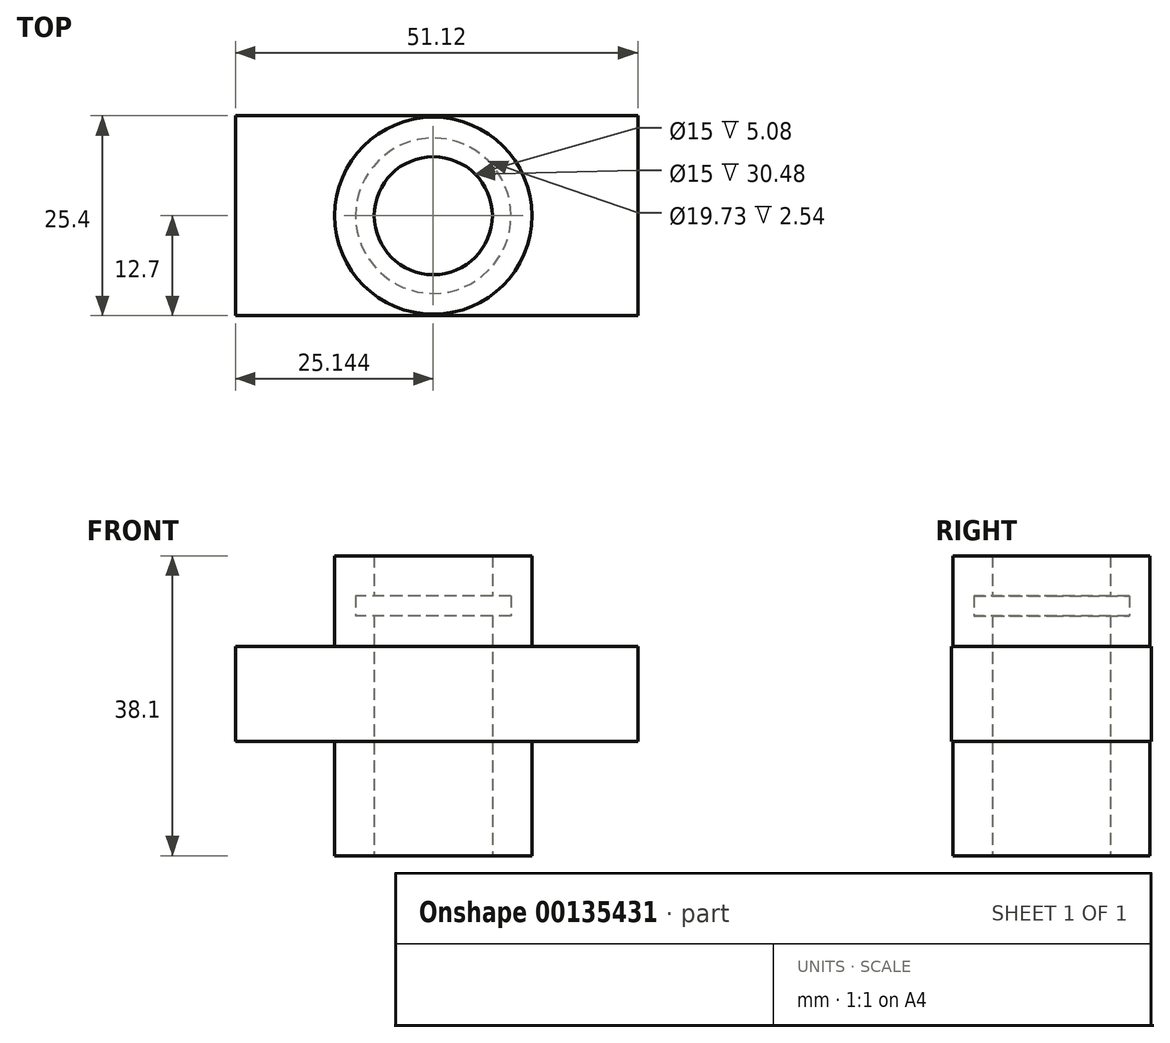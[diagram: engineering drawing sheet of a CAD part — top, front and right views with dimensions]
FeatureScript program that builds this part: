
annotation { "Feature Type Name" : "Feature", "Feature Type Description" : "" }
export const myFeature = defineFeature(function(context is Context, id is Id, definition is map)
    precondition{}
    {
        {
            var Q0;
            Q0=qCreatedBy(makeId("Front.planeOp"),FACE);
            var sketch = newSketch(context, id + "F0", { "sketchPlane" : qUnion([Q0])});
            skLineSegment(sketch, "E0", {"start": v(0, 0) * mm, "end": v(0, 14.5) * mm, "construction": true});
            skLineSegment(sketch, "E1", {"start": v(0, 14.5) * mm, "end": v(-9.8, 14.5) * mm});
            skLineSegment(sketch, "E2", {"start": v(-9.8, 14.5) * mm, "end": v(-9.8, 26.6) * mm});
            skLineSegment(sketch, "E3", {"start": v(-9.8, 26.6) * mm, "end": v(0, 26.6) * mm});
            skLineSegment(sketch, "E4", {"start": v(0, 26.6) * mm, "end": v(0, 40.16) * mm, "construction": true});
            skLineSegment(sketch, "E5", {"start": v(0, 40.16) * mm, "end": v(31.5, 40.16) * mm, "construction": true});
            skLineSegment(sketch, "E6", {"start": v(31.5, 40.16) * mm, "end": v(31.5, 26.6) * mm, "construction": true});
            skLineSegment(sketch, "E7", {"start": v(31.5, 26.6) * mm, "end": v(41.3, 26.6) * mm});
            skLineSegment(sketch, "E8", {"start": v(41.3, 26.6) * mm, "end": v(41.3, 14.5) * mm});
            skLineSegment(sketch, "E9", {"start": v(41.3, 14.5) * mm, "end": v(31.5, 14.5) * mm});
            skLineSegment(sketch, "E10", {"start": v(31.5, 14.5) * mm, "end": v(31.5, 0) * mm, "construction": true});
            skLineSegment(sketch, "E11", {"start": v(31.5, 0) * mm, "end": v(0, 0) * mm, "construction": true});
            skLineSegment(sketch, "E12", {"start": v(0, 26.6) * mm, "end": v(31.5, 26.6) * mm});
            skLineSegment(sketch, "E13", {"start": v(0, 14.5) * mm, "end": v(31.5, 14.5) * mm});
            skSolve(sketch);
        }
        {
            var Q0;
            Q0 = qSketchRegion(id + "F0", true);
            extrude(context, id + "F1", {"entities" : qUnion([Q0]), "depth" : 25.4 * mm});
        }
        {
            var Q0;
            Q0=qCreatedBy(makeId("Top.planeOp"),FACE);
            var sketch = newSketch(context, id + "F2", { "sketchPlane" : qUnion([Q0])});
            skCircle(sketch, "E14", {"center": v(15.33, -12.7) * mm, "radius": 7.5 * mm});
            skCircle(sketch, "E15", {"center": v(15.33, -12.7) * mm, "radius": 12.51 * mm});
            skSolve(sketch);
        }
        {
            var Q0;
            Q0 = qSketchRegion(id + "F2", true);
            extrude(context, id + "F3", {"entities" : qUnion([Q0]), "operationType" : NewBodyOperationType.ADD, "depth" : 38.1 * mm});
        }
        {
            var Q0;
            Q0=qCreatedBy(makeId("Top.planeOp"),FACE);
            var sketch = newSketch(context, id + "F4", { "sketchPlane" : qUnion([Q0])});
            skCircle(sketch, "E16", {"center": v(15.33, -12.7) * mm, "radius": 9.87 * mm});
            skSolve(sketch);
        }
        {
            var Q0;
            Q0 = qSketchRegion(id + "F4", true);
            extrude(context, id + "F5", {"entities" : qUnion([Q0]), "operationType" : NewBodyOperationType.REMOVE, "depth" : 33.02 * mm, "hasSecondDirection" : true, "secondDirectionOppositeDirection" : false, "secondDirectionDepth" : 30.48 * mm});
        }
        {
            var Q0;
            Q0=qCreatedBy(makeId("Top.planeOp"),FACE);
            var sketch = newSketch(context, id + "F6", { "sketchPlane" : qUnion([Q0])});
            skCircle(sketch, "E17", {"center": v(15.33, -12.7) * mm, "radius": 7.5 * mm});
            skSolve(sketch);
        }
        {
            var Q0;
            Q0 = qSketchRegion(id + "F6", true);
            extrude(context, id + "F7", {"entities" : qUnion([Q0]), "operationType" : NewBodyOperationType.REMOVE, "endBound" : BoundingType.THROUGH_ALL, "depth" : 25.4 * mm});
        }
    });
